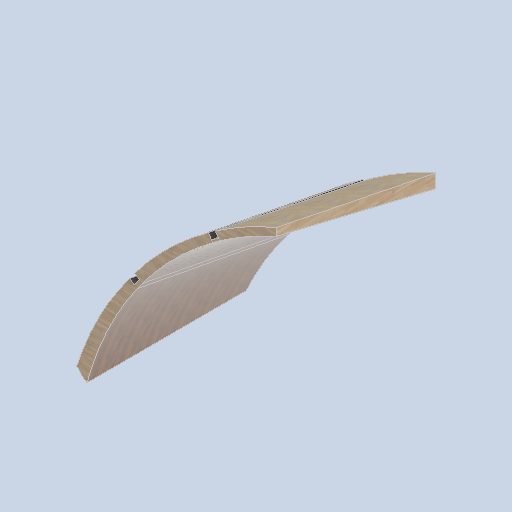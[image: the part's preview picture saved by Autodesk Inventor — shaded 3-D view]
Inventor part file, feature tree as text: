
AUTODESK INVENTOR PART (.ipt)
format: ipt  version: 2024.2 (Build 282272000, 272)  size: 252,416 bytes
history: native  units: in
note: dims shown in document units (in); Inventor stores cm internally (conversion verified against a paired STEP export)
features: sketch x7, other x3, plane x2
ambient origin geometry x8: Origin, YZ Plane, XZ Plane, XY Plane, X Axis, Y Axis, Z Axis, Center Point
bodies: Solid1 (feature_tree)
feature tree (12):
  other  "panel_block_01_MIR.ipt"
  other  "Solid1::panel_block_01_MIR.ipt"
  other  "TaggingFeature1"
  sketch  "Sketch3"  dims[d0=0.3937in]
  sketch  "Sketch8"
  sketch  "Sketch9"
  sketch  "Sketch10"
  sketch  "Sketch11"
  sketch  "Sketch14"
  sketch  "Sketch15"
  plane  "Work Plane1"
  plane  "Work Plane2"
